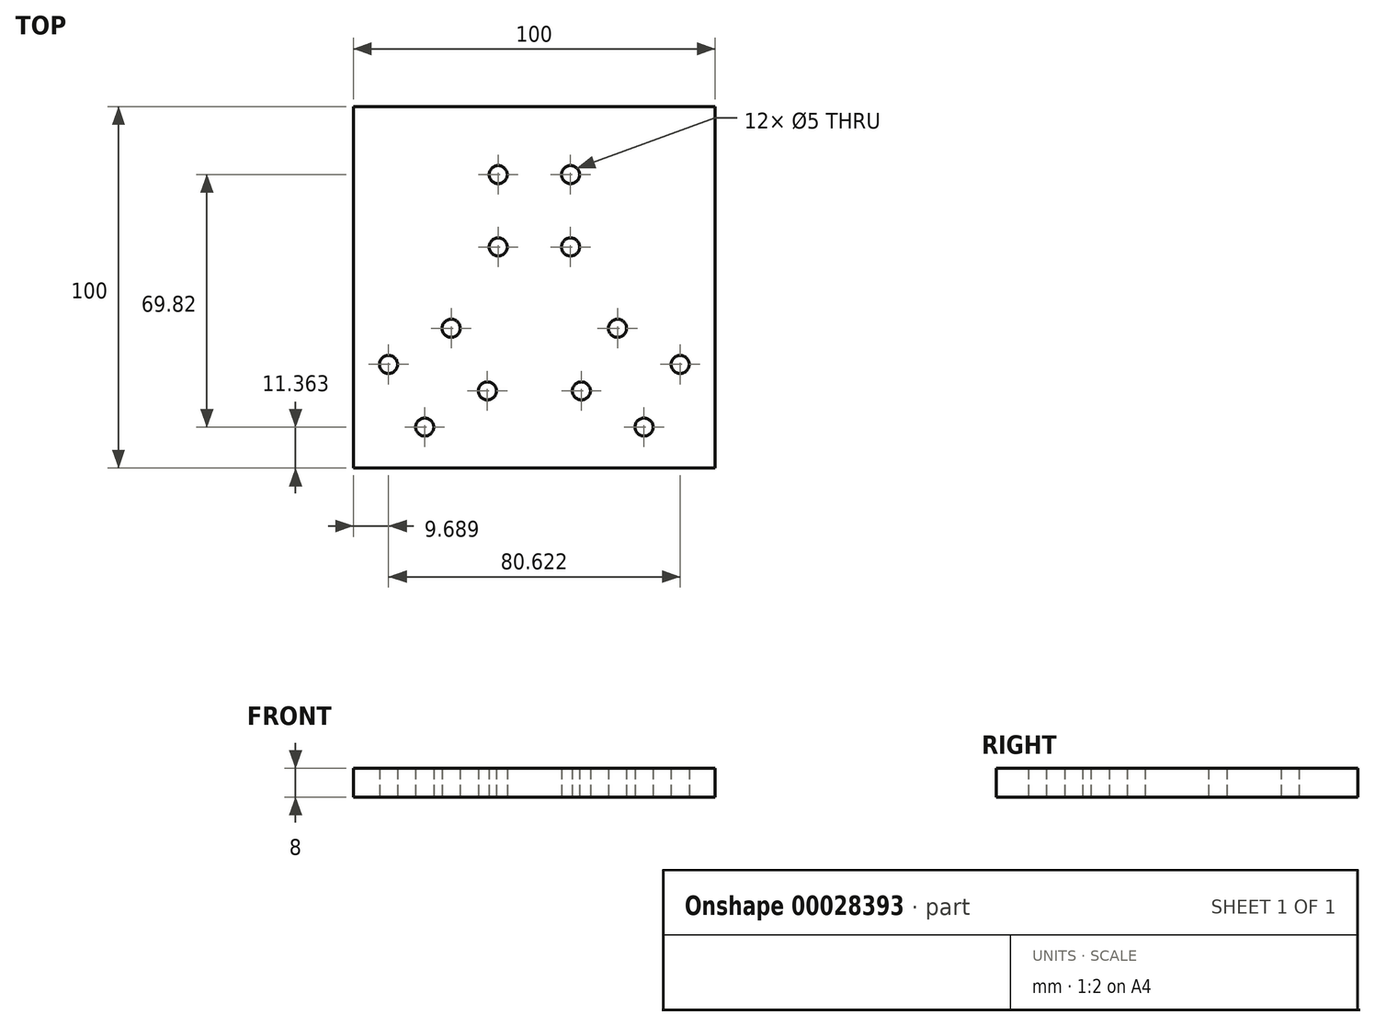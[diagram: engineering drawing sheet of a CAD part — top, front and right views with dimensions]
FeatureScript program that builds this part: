
annotation { "Feature Type Name" : "Feature", "Feature Type Description" : "" }
export const myFeature = defineFeature(function(context is Context, id is Id, definition is map)
    precondition{}
    {
        {
            var Q0;
            Q0=qCreatedBy(makeId("Top.planeOp"),FACE);
            var sketch = newSketch(context, id + "F0", { "sketchPlane" : qUnion([Q0])});
            skLineSegment(sketch, "E0", {"start": v(0, 0) * mm, "end": v(0, 59.59) * mm, "construction": true});
            skLineSegment(sketch, "E1", {"start": v(0, 0) * mm, "end": v(-50, -28.87) * mm, "construction": true});
            skLineSegment(sketch, "E2", {"start": v(0, 0) * mm, "end": v(50, -28.87) * mm, "construction": true});
            skLineSegment(sketch, "E3", {"start": v(-10, 59.59) * mm, "end": v(-10, 5.77) * mm, "construction": true});
            skLineSegment(sketch, "E4", {"start": v(10, 59.59) * mm, "end": v(10, 5.77) * mm, "construction": true});
            skLineSegment(sketch, "E5", {"start": v(-50, -17.32) * mm, "end": v(-10, 5.77) * mm, "construction": true});
            skLineSegment(sketch, "E6", {"start": v(50, -17.32) * mm, "end": v(10, 5.77) * mm, "construction": true});
            skLineSegment(sketch, "E7", {"start": v(-50, -40.41) * mm, "end": v(0, -11.55) * mm, "construction": true});
            skLineSegment(sketch, "E8", {"start": v(50, -40.41) * mm, "end": v(0, -11.55) * mm, "construction": true});
            skPoint(sketch, "E9.center", {"position": v(0, 0) * mm});
            skLineSegment(sketch, "E10.rect.bottom", {"start": v(-50, 59.59) * mm, "end": v(50, 59.59) * mm});
            skLineSegment(sketch, "E10.rect.left", {"start": v(-50, 59.59) * mm, "end": v(-50, -40.41) * mm});
            skLineSegment(sketch, "E10.rect.right", {"start": v(50, 59.59) * mm, "end": v(50, -40.41) * mm});
            skLineSegment(sketch, "E11", {"start": v(-50, -40.41) * mm, "end": v(50, -40.41) * mm});
            skCircle(sketch, "E12", {"center": v(-10, 20.77) * mm, "radius": 2.5 * mm});
            skCircle(sketch, "E13", {"center": v(-10, 40.77) * mm, "radius": 2.5 * mm});
            skCircle(sketch, "E14.MirrorC", {"center": v(10, 20.77) * mm, "radius": 2.5 * mm});
            skCircle(sketch, "E15.MirrorC", {"center": v(10, 40.77) * mm, "radius": 2.5 * mm});
            skCircle(sketch, "E16.1.0", {"center": v(-30.31, -29.05) * mm, "radius": 2.5 * mm});
            skCircle(sketch, "E16.1.1", {"center": v(-13, -19.05) * mm, "radius": 2.5 * mm});
            skCircle(sketch, "E16.1.2", {"center": v(-23, -1.73) * mm, "radius": 2.5 * mm});
            skCircle(sketch, "E16.1.3", {"center": v(-40.31, -11.73) * mm, "radius": 2.5 * mm});
            skCircle(sketch, "E16.2.0", {"center": v(40.31, -11.73) * mm, "radius": 2.5 * mm});
            skCircle(sketch, "E16.2.1", {"center": v(23, -1.73) * mm, "radius": 2.5 * mm});
            skCircle(sketch, "E16.2.2", {"center": v(13, -19.05) * mm, "radius": 2.5 * mm});
            skCircle(sketch, "E16.2.3", {"center": v(30.31, -29.05) * mm, "radius": 2.5 * mm});
            skLineSegment(sketch, "E17", {"start": v(-50, 9.59) * mm, "end": v(50, 9.59) * mm});
            skPoint(sketch, "E18", {"position": v(0, 9.59) * mm});
            skSolve(sketch);
        }
        {
            var Q0;
            Q0 = qSketchRegion(id + "F0", true);
            extrude(context, id + "F1", {"entities" : qUnion([Q0]), "depth" : 8 * mm});
        }
    });
